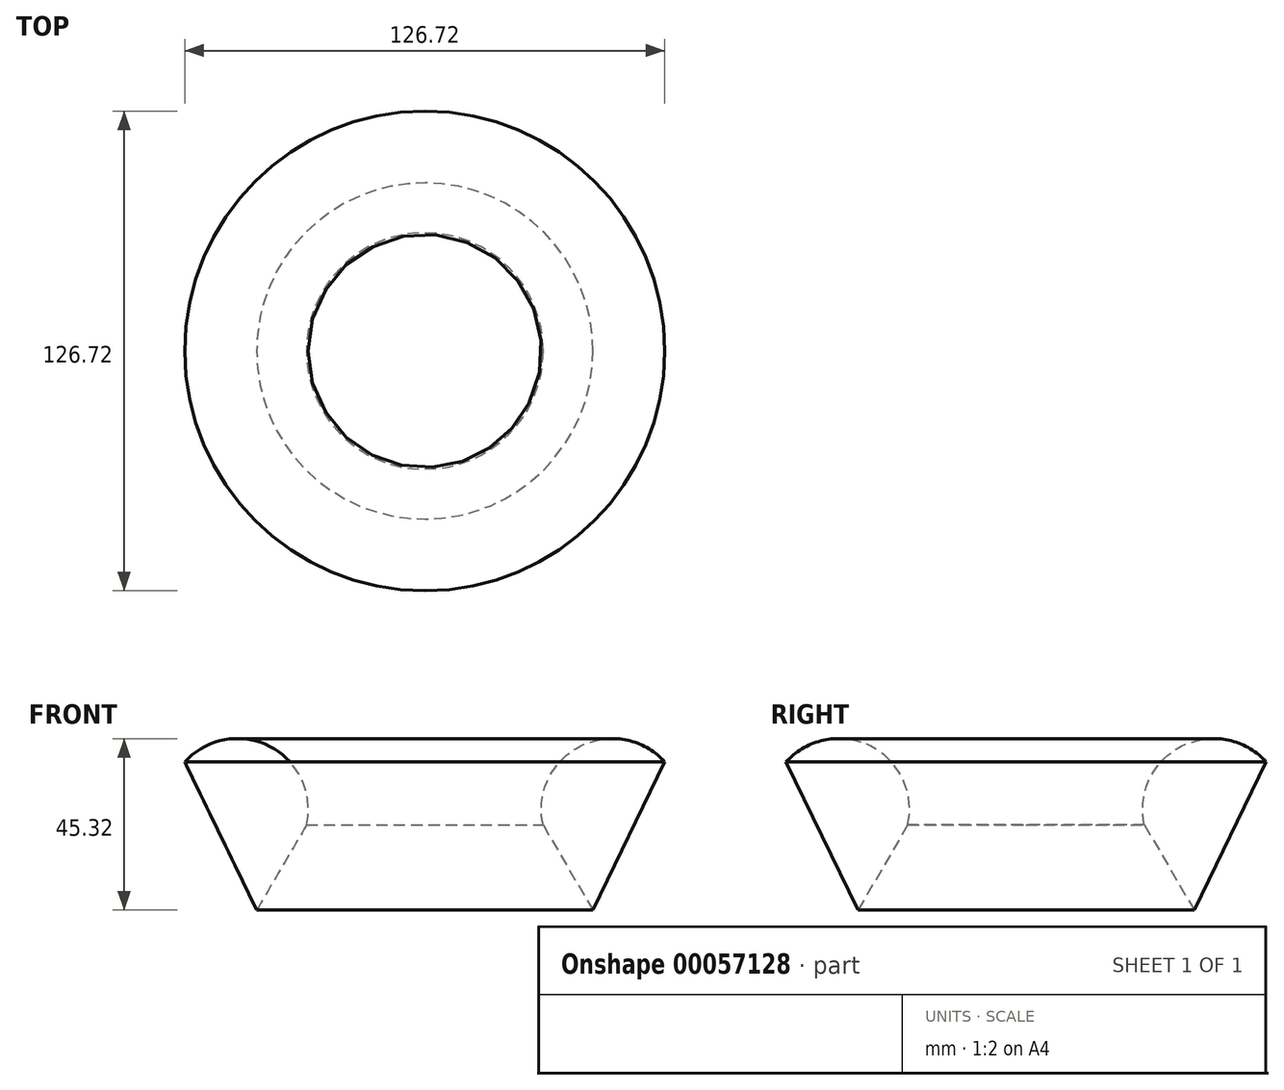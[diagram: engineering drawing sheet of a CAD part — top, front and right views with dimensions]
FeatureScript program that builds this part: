
annotation { "Feature Type Name" : "Feature", "Feature Type Description" : "" }
export const myFeature = defineFeature(function(context is Context, id is Id, definition is map)
    precondition{}
    {
        {
            var Q0;
            Q0=qCreatedBy(makeId("Front.planeOp"),FACE);
            var sketch = newSketch(context, id + "F0", { "sketchPlane" : qUnion([Q0])});
            skLineSegment(sketch, "E0", {"start": v(-63.36, 42.48) * mm, "end": v(-44.38, 3.36) * mm});
            skLineSegment(sketch, "E1", {"start": v(-44.38, 3.36) * mm, "end": v(-31.24, 25.84) * mm});
            skArc(sketch, "E2", {"start": v(-31.24, 25.84) * mm, "mid": v(-40.86, 46.58) * mm, "end": v(-63.36, 42.48) * mm});
            skSolve(sketch);
        }
        {
            var Q0;
            Q0=qCreatedBy(makeId("Front.planeOp"),FACE);
            var sketch = newSketch(context, id + "F1", { "sketchPlane" : qUnion([Q0])});
            skLineSegment(sketch, "E3", {"start": v(0, 0) * mm, "end": v(0, 111.68) * mm, "construction": true});
            skSolve(sketch);
        }
        {
            var Q0;
            Q0=makeQuery(id+"F0.imprint","IMPRINT",FACE,{"disambiguationData":[TD([[makeQuery(id+"F0.imprint","IMPRINT",EDGE,{"derivedFrom":sQuery(id+"F0.wireOp",EDGE,"E0")}),1.0]])]});
            var Q1;
            Q1=sQuery(id+"F1.wireOp",EDGE,"E3");
            revolve(context, id + "F2", {"entities" : qUnion([Q0]), "axis" : qUnion([Q1]), "revolveType" : RevolveType.FULL});
        }
    });
